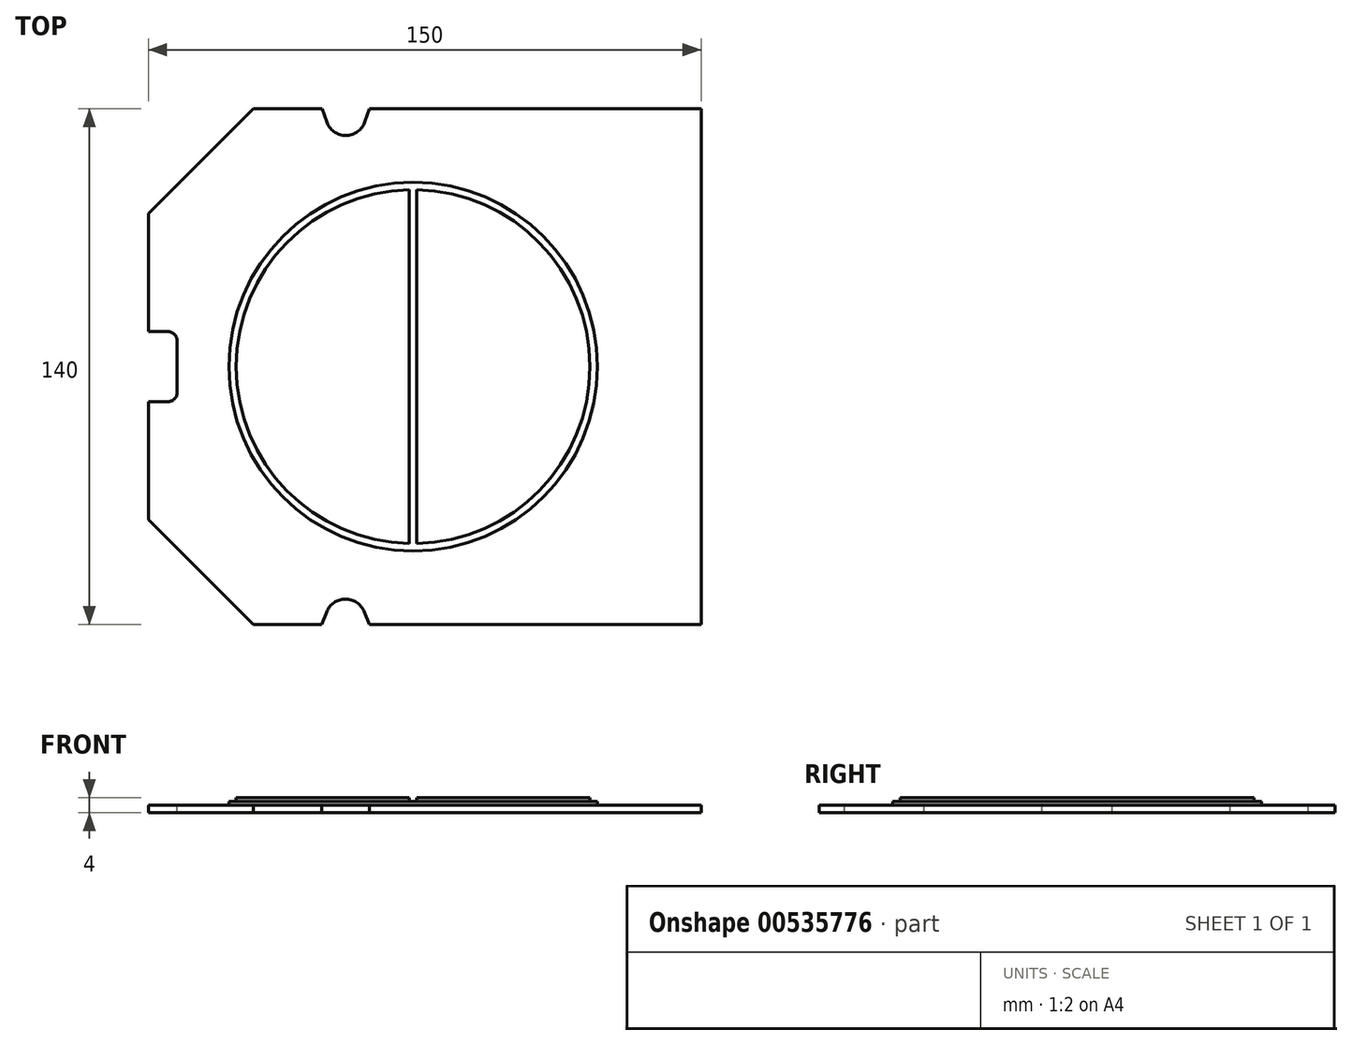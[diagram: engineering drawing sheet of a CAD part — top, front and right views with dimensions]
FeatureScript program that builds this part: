
annotation { "Feature Type Name" : "Feature", "Feature Type Description" : "" }
export const myFeature = defineFeature(function(context is Context, id is Id, definition is map)
    precondition{}
    {
        {
            var Q0;
            Q0=qCreatedBy(makeId("Top.planeOp"),FACE);
            var sketch = newSketch(context, id + "F0", { "sketchPlane" : qUnion([Q0])});
            skLineSegment(sketch, "E0.bottom", {"start": v(75, -70) * mm, "end": v(-75, -70) * mm});
            skLineSegment(sketch, "E0.top", {"start": v(75, 70) * mm, "end": v(-75, 70) * mm});
            skLineSegment(sketch, "E0.left", {"start": v(75, -70) * mm, "end": v(75, 70) * mm});
            skLineSegment(sketch, "E0.right", {"start": v(-75, -70) * mm, "end": v(-75, 70) * mm});
            skPoint(sketch, "E0.middle", {"position": v(0, 0) * mm});
            skSolve(sketch);
        }
        {
            var Q0;
            Q0=qSketchRegion(id+"F0",true);
            extrude(context, id + "F1", {"entities" : qUnion([Q0]), "depth" : 2 * mm, "offsetDistance" : 25 * mm});
        }
        {
            var Q0;
            Q0=makeQuery(id+"F1.opExtrude","CAP_FACE",FACE,{"disambiguationData":[OSD([sQuery(id+"F0.wireOp",EDGE,"E0.bottom"),sQuery(id+"F0.wireOp",EDGE,"E0.top"),sQuery(id+"F0.wireOp",EDGE,"E0.left"),sQuery(id+"F0.wireOp",EDGE,"E0.right")])],"isStart":false});
            var sketch = newSketch(context, id + "F2", { "sketchPlane" : qUnion([Q0])});
            skLineSegment(sketch, "E1", {"start": v(-75, 41.5) * mm, "end": v(-46.5, 70) * mm});
            skLineSegment(sketch, "E2", {"start": v(-75, -41.5) * mm, "end": v(-46.5, -70) * mm});
            skSolve(sketch);
        }
        {
            var Q0;
            Q0=qSketchRegion(id+"F2",true);
            var Q1;
            {var subQ0=sQuery(id+"F2.wireOp",EDGE,"E1");Q1=makeQuery(id+"F2.imprint","IMPRINT",FACE,{"disambiguationData":[TD([[makeQuery(id+"F2.imprint","IMPRINT",EDGE,{"derivedFrom":subQ0}),1.0]])]});}
            var Q2;
            {var subQ0=sQuery(id+"F2.wireOp",EDGE,"E2");Q2=makeQuery(id+"F2.imprint","IMPRINT",FACE,{"disambiguationData":[TD([[makeQuery(id+"F2.imprint","IMPRINT",EDGE,{"derivedFrom":subQ0}),-1.0]])]});}
            extrude(context, id + "F3", {"entities" : qUnion([Q0, Q1, Q2]), "operationType" : NewBodyOperationType.REMOVE, "endBound" : BoundingType.THROUGH_ALL, "oppositeDirection" : true, "depth" : 25 * mm, "offsetDistance" : 25 * mm});
        }
        {
            var Q0;
            Q0=makeQuery(id+"F1.opExtrude","CAP_FACE",FACE,{"disambiguationData":[OSD([sQuery(id+"F0.wireOp",EDGE,"E0.bottom"),sQuery(id+"F0.wireOp",EDGE,"E0.top"),sQuery(id+"F0.wireOp",EDGE,"E0.left"),sQuery(id+"F0.wireOp",EDGE,"E0.right")])],"isStart":false});
            var sketch = newSketch(context, id + "F4", { "sketchPlane" : qUnion([Q0])});
            skLineSegment(sketch, "E3", {"start": v(-75, 9.5) * mm, "end": v(-69.68, 9.5) * mm});
            skLineSegment(sketch, "E4", {"start": v(-67.18, 7) * mm, "end": v(-67.18, -7) * mm});
            skArc(sketch, "E5", {"start": v(-67.18, 7) * mm, "mid": v(-67.91, 8.77) * mm, "end": v(-69.68, 9.5) * mm});
            skLineSegment(sketch, "E6", {"start": v(-75, -9.5) * mm, "end": v(-69.68, -9.5) * mm});
            skArc(sketch, "E7", {"start": v(-69.68, -9.5) * mm, "mid": v(-67.91, -8.77) * mm, "end": v(-67.18, -7) * mm});
            skSolve(sketch);
        }
        {
            var Q0;
            Q0=qSketchRegion(id+"F4",true);
            var Q1;
            {var subQ1=sQuery(id+"F4.wireOp",EDGE,"E3");Q1=makeQuery(id+"F4.imprint","IMPRINT",FACE,{"disambiguationData":[TD([[makeQuery(id+"F4.imprint","IMPRINT",EDGE,{"derivedFrom":subQ1}),-1.0]])]});}
            extrude(context, id + "F5", {"entities" : qUnion([Q0, Q1]), "operationType" : NewBodyOperationType.REMOVE, "endBound" : BoundingType.THROUGH_ALL, "oppositeDirection" : true, "depth" : 25 * mm, "offsetDistance" : 25 * mm});
        }
        {
            var Q0;
            Q0=makeQuery(id+"F1.opExtrude","CAP_FACE",FACE,{"disambiguationData":[OSD([sQuery(id+"F0.wireOp",EDGE,"E0.bottom"),sQuery(id+"F0.wireOp",EDGE,"E0.top"),sQuery(id+"F0.wireOp",EDGE,"E0.left"),sQuery(id+"F0.wireOp",EDGE,"E0.right")])],"isStart":false});
            var sketch = newSketch(context, id + "F6", { "sketchPlane" : qUnion([Q0])});
            skArc(sketch, "E8", {"start": v(-26.63, 66.43) * mm, "mid": v(-21.44, 62.74) * mm, "end": v(-16.24, 66.43) * mm});
            skArc(sketch, "E9", {"start": v(-16.42, -66.5) * mm, "mid": v(-21.52, -63.06) * mm, "end": v(-26.61, -66.5) * mm});
            skLineSegment(sketch, "E10", {"start": v(-27.88, 70) * mm, "end": v(-26.63, 66.43) * mm});
            skLineSegment(sketch, "E11", {"start": v(-15, 70) * mm, "end": v(-16.24, 66.43) * mm});
            skLineSegment(sketch, "E12", {"start": v(-26.61, -66.5) * mm, "end": v(-28.03, -70) * mm});
            skLineSegment(sketch, "E13", {"start": v(-16.42, -66.5) * mm, "end": v(-15, -70) * mm});
            skSolve(sketch);
        }
        {
            var Q0;
            Q0=qSketchRegion(id+"F6",true);
            var Q1;
            Q1=makeQuery(id+"F6.imprint","IMPRINT",FACE,{"disambiguationData":[TD([[makeQuery(id+"F6.imprint","IMPRINT",EDGE,{"derivedFrom":sQuery(id+"F6.wireOp",EDGE,"E9")}),1.0]])]});
            var Q2;
            Q2=makeQuery(id+"F6.imprint","IMPRINT",FACE,{"disambiguationData":[TD([[makeQuery(id+"F6.imprint","IMPRINT",EDGE,{"derivedFrom":sQuery(id+"F6.wireOp",EDGE,"E8")}),1.0]])]});
            extrude(context, id + "F7", {"entities" : qUnion([Q0, Q1, Q2]), "operationType" : NewBodyOperationType.REMOVE, "endBound" : BoundingType.THROUGH_ALL, "oppositeDirection" : true, "depth" : 25 * mm, "offsetDistance" : 25 * mm});
        }
        {
            var Q0;
            Q0=makeQuery(id+"F1.opExtrude","CAP_FACE",FACE,{"disambiguationData":[OSD([sQuery(id+"F0.wireOp",EDGE,"E0.bottom"),sQuery(id+"F0.wireOp",EDGE,"E0.top"),sQuery(id+"F0.wireOp",EDGE,"E0.left"),sQuery(id+"F0.wireOp",EDGE,"E0.right")])],"isStart":false});
            var sketch = newSketch(context, id + "F8", { "sketchPlane" : qUnion([Q0])});
            skCircle(sketch, "E14", {"center": v(-3.16, 0) * mm, "radius": 50 * mm});
            skPoint(sketch, "E14.first.point", {"position": v(-36.36, 37.39) * mm});
            skPoint(sketch, "E14.second.point", {"position": v(32.35, -35.2) * mm});
            skPoint(sketch, "E14.third.point", {"position": v(42.82, 19.64) * mm});
            skSolve(sketch);
        }
        {
            var Q0;
            Q0=qSketchRegion(id+"F8",true);
            extrude(context, id + "F9", {"entities" : qUnion([Q0]), "operationType" : NewBodyOperationType.ADD, "depth" : 1 * mm, "offsetDistance" : 25 * mm});
        }
        {
            var Q0;
            Q0=makeQuery(id+"F9.opExtrude","CAP_FACE",FACE,{"disambiguationData":[OSD([sQuery(id+"F8.wireOp",EDGE,"E14")])],"isStart":false});
            var sketch = newSketch(context, id + "F10", { "sketchPlane" : qUnion([Q0])});
            skCircle(sketch, "E15", {"center": v(-3.16, 0) * mm, "radius": 48 * mm});
            skLineSegment(sketch, "E16", {"start": v(-4.16, 47.99) * mm, "end": v(-4.16, -47.99) * mm});
            skLineSegment(sketch, "E17", {"start": v(-2.16, 47.99) * mm, "end": v(-2.16, -47.99) * mm});
            skSolve(sketch);
        }
        {
            var Q0;
            {var subQ0=sQuery(id+"F10.wireOp",EDGE,"E17");Q0=makeQuery(id+"F10.imprint","IMPRINT",FACE,{"disambiguationData":[TD([[makeQuery(id+"F10.imprint","IMPRINT",EDGE,{"derivedFrom":subQ0}),1.0]])]});}
            var Q1;
            {var subQ0=sQuery(id+"F10.wireOp",EDGE,"E16");Q1=makeQuery(id+"F10.imprint","IMPRINT",FACE,{"disambiguationData":[TD([[makeQuery(id+"F10.imprint","IMPRINT",EDGE,{"derivedFrom":subQ0}),-1.0]])]});}
            extrude(context, id + "F11", {"entities" : qUnion([Q0, Q1]), "operationType" : NewBodyOperationType.ADD, "depth" : 1 * mm, "offsetDistance" : 25 * mm});
        }
    });
